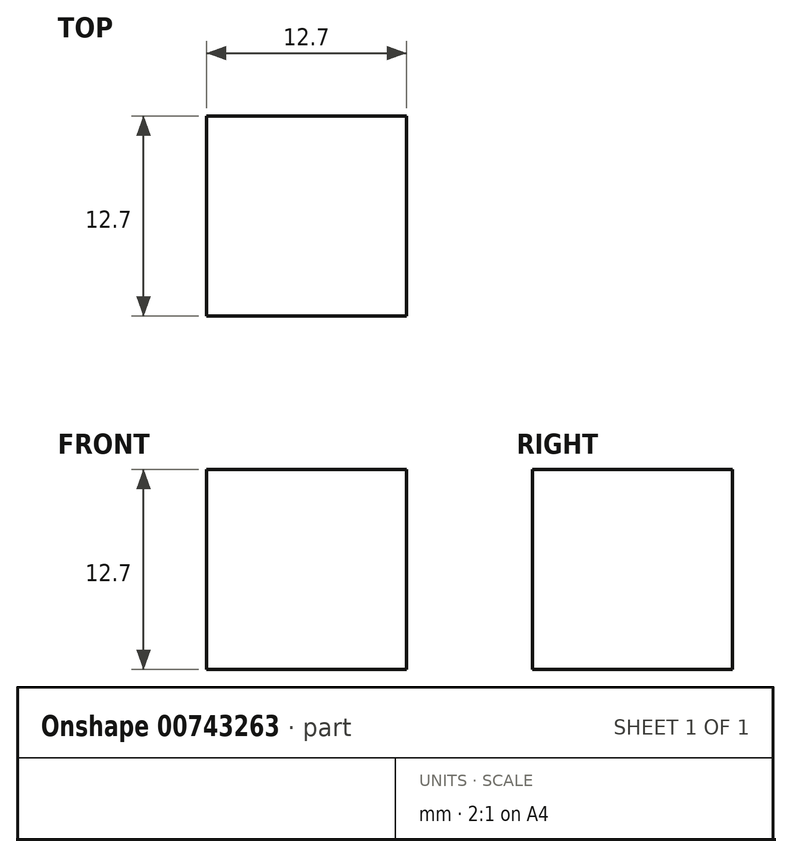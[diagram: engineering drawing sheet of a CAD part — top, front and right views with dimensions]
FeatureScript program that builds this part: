
annotation { "Feature Type Name" : "Feature", "Feature Type Description" : "" }
export const myFeature = defineFeature(function(context is Context, id is Id, definition is map)
    precondition{}
    {
        {
            var Q0;
            Q0=qCreatedBy(makeId("Top.planeOp"),FACE);
            var sketch = newSketch(context, id + "F0", { "sketchPlane" : qUnion([Q0])});
            skLineSegment(sketch, "E0.bottom", {"start": v(0, 0) * mm, "end": v(12.7, 0) * mm});
            skLineSegment(sketch, "E0.top", {"start": v(0, 12.7) * mm, "end": v(12.7, 12.7) * mm});
            skLineSegment(sketch, "E0.left", {"start": v(0, 0) * mm, "end": v(0, 12.7) * mm});
            skLineSegment(sketch, "E0.right", {"start": v(12.7, 0) * mm, "end": v(12.7, 12.7) * mm});
            skSolve(sketch);
        }
        {
            var Q0;
            Q0=makeQuery(id+"F0.imprint","IMPRINT",FACE,{"disambiguationData":[TD([[makeQuery(id+"F0.imprint","IMPRINT",EDGE,{"derivedFrom":sQuery(id+"F0.wireOp",EDGE,"E0.bottom")}),1.0]])]});
            extrude(context, id + "F1", {"entities" : qUnion([Q0]), "depth" : 12.7 * mm, "offsetDistance" : 25.4 * mm});
        }
    });
